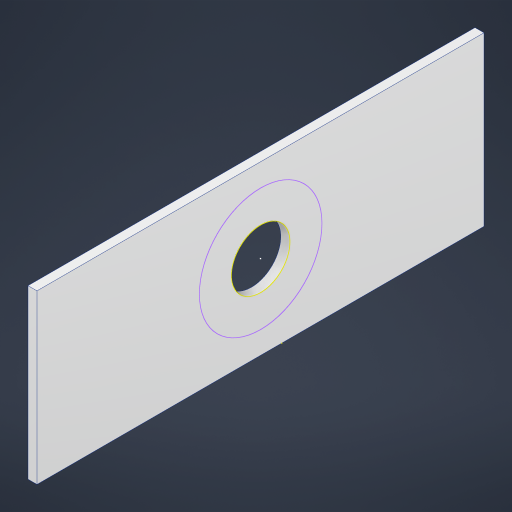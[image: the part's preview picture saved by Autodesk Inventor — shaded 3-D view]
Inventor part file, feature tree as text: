
AUTODESK INVENTOR PART (.ipt)
format: ipt  version: 2024 (Build 280153000, 153)  size: 181,248 bytes
history: native  units: mm
features: sketch x3, extrude x2, projected_geometry x1
ambient origin geometry x8: Origin, YZ Plane, XZ Plane, XY Plane, X Axis, Y Axis, Z Axis, Center Point
bodies: Solid1 (feature_tree)
feature tree (6):
  extrude  "Extrusion1"  Depth=496.0mm
  extrude  "Extrusion5"  Depth=186.0mm
  sketch  "Sketch4"  dims[d17=186.0mm d18=0.0mm d19=93.0mm d20=248.0mm d21=248.0mm d22=93.0mm]
  sketch  "Sketch1"  dims[d0=10.0mm d1=496.0mm]
  sketch  "Sketch3"  dims[d2=186.0mm d3=0.0mm d16=65.0mm]
  projected_geometry  "Projected Loop1"
